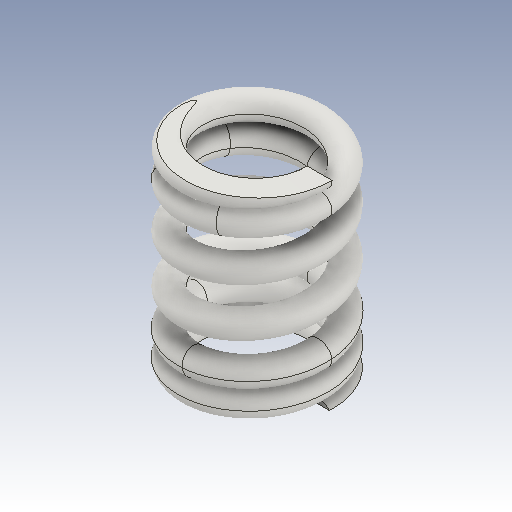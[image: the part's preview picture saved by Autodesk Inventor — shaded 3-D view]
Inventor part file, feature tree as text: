
AUTODESK INVENTOR PART (.ipt)
format: ipt  version: 2023.3 (Build 273359000, 359)  size: 781,824 bytes
history: native  units: mm
features: other x65, extrude x8, plane x5, helix x3, sketch x3, sweep x2
ambient origin geometry x8: Origin, YZ Plane, XZ Plane, XY Plane, X Axis, Y Axis, Z Axis, Center Point
bodies: Solid1 (feature_tree)
feature tree (86):
  other  "Hauptschraubenpfad(Rechts)"
  other  "Profilarbeitsebene(Rechts)"
  plane  "Arbeitsebene(Rechts) starten"
  plane  "Arbeitsebene(Rechts) beenden"
  other  "Schnittarbeitsebene(Rechts) beenden"
  other  "Schnittarbeitsebene(Rechts) starten"
  other  "Schnittarbeitsebene mit flachen Enden 1(Rechts)"
  other  "Schnittarbeitsebene mit flachen Enden 2(Rechts)"
  sweep  "Main Coil Feature(R)"
  other  "Übergangsschraube 1(Rechts) starten"
  helix  "Coil  Start Transition 2(R)"  [1 undecoded]
  helix  "Coil  Start Transition 3(R)"  [1 undecoded]
  helix  "Coil  Start Transition 4(R)"  [1 undecoded]
  other  "Endenschraube(Rechts) starten"
  extrude  "Schnittelement(Rechts) starten"  Depth=10.0mm
  other  "Übergangsschraube 1(Rechts) beenden"
  other  "Übergangsschraube 2(Rechts) beenden"
  other  "Übergangsschraube 3(Rechts) beenden"
  other  "Übergangsschraube 4(Rechts) beenden"
  other  "Spirale(Rechts) beenden"
  extrude  "Schnittelement(Rechts) beenden"  Depth=10.0mm
  extrude  "Schnittelement mit flachen Enden 1(Rechts)"  Depth=10.0mm
  extrude  "Plain Ends Cut  2(R)"  Depth=10.0mm TaperAngle=0.0deg
  other  "Hauptschraubenpfad(Links)"
  other  "Profilarbeitsebene(Links)"
  plane  "Arbeitsebene(Links) starten"
  plane  "Arbeitsebene(Links) beenden"
  other  "Schnittarbeitsebene(Links) beenden"
  other  "Schnittarbeitsebene(Links) starten"
  other  "Schnittarbeitsebene mit flachen Enden 1(Links)"
  other  "Schnittarbeitsebene mit flachen Enden 2(Links)"
  sweep  "Main Coil Feature(L)"
  other  "Übergangsschraube 1(Links) starten"
  other  "Übergangsschraube 2(Links) starten"
  other  "Übergangsschraube 3(Links) starten"
  other  "Übergangsschraube 4(Links) starten"
  other  "Endenschraube(Links) starten"
  extrude  "Schnittelement(Links) starten"  Depth=10.0mm TaperAngle=0.0deg
  other  "Übergangsschraube 1(Links) beenden"
  other  "Übergangsschraube 2(Links) beenden"
  other  "Übergangsschraube 3(Links) beenden"
  other  "Übergangsschraube 4(Links) beenden"
  other  "Spirale(Links) beenden"
  extrude  "Schnittelement(Links) beenden"  Depth=10.0mm
  extrude  "Cut Plain Ends Cut 1(L)"  TaperAngle=0.0deg  [1 undecoded]
  extrude  "Cut Plain Ends Cut 2(L)"  TaperAngle=0.0deg  [1 undecoded]
  other  "iMate-basierte Arbeitsebene"
  other  "Vorschau Mittelpunkt"
  other  "Vorschau X-Achse"
  other  "Pfadprofilskizze(Rechts)"
  other  "Srf1"
  other  "Spiralenprofilskizze(Rechts)"
  other  "Übergangsschraubenskizze 1(Rechts) starten"
  sketch  "Sketch  Start Transition 2(R)"  dims[d0=0.125mm d2=0.967126mm d3=10.0mm d4=17.5mm]
  sketch  "Sketch  Start Transition 3(R)"  dims[d5=0.0mm d6=90.0deg d7=90.0deg d8=0.0mm d9=0.0mm d12=1.006393mm d13=-1.301131mm d14=0.5mm]
  sketch  "Sketch  Start Transition 4(R)"  dims[d15=0.0mm d16=0.850345mm d17=10.0mm d18=2.5mm d19=0.0mm d20=90.0deg d21=90.0deg d22=0.0mm d23=0.0mm d24=0.733563mm d25=10.0mm d26=2.5mm d27=0.0mm d28=90.0deg d29=90.0deg d30=0.0mm d31=0.0mm d32=0.616782mm d33=10.0mm d34=2.5mm d35=0.0mm d36=90.0deg d37=90.0deg d38=0.0mm d39=0.0mm d40=0.5mm d41=10.0mm d42=2.5mm d43=0.0mm d44=90.0deg d45=90.0deg d46=0.0mm d47=0.0mm d48=0.850345mm d49=10.0mm d50=1.875mm d51=0.0mm d52=90.0deg d53=90.0deg d54=0.0mm d55=0.0mm d56=0.733563mm d57=10.0mm d58=1.875mm d59=0.0mm d60=90.0deg d61=90.0deg d62=0.0mm d63=0.0mm d64=0.616782mm d65=10.0mm d66=1.875mm d67=0.0mm d68=90.0deg d69=90.0deg d70=0.0mm d71=0.0mm d72=0.5mm d73=10.0mm d74=1.875mm d75=0.0mm d76=90.0deg d77=90.0deg d78=0.0mm d79=0.0mm d81=10.0mm d82=15.0mm d83=0.0mm d84=90.0deg d85=90.0deg d86=0.0mm d87=0.0mm d88=0.503777mm d89=10.0mm d90=10.0mm d91=0.0mm d92=90.0deg d93=90.0deg d94=0.0mm d95=0.0mm d96=3.0mm d97=0.503777mm d98=0.0mm d99=3.0mm d100=0.503777mm d101=0.0mm d102=0.0mm d103=0.0mm d104=0.0mm d105=0.0mm d106=0.0mm d108=0.0mm d112=0.0mm d113=0.0mm d114=0.0mm d121=0.129706mm d131=0.0mm d132=0.0mm d133=0.0mm d134=0.0mm d135=0.125mm d137=0.967126mm d138=10.0mm d139=17.5mm d140=0.0mm d141=90.0deg d142=90.0deg d143=0.0mm d144=0.0mm d145=1.006393mm d146=-1.301131mm d147=0.129706mm d148=0.003762mm d149=0.5mm d150=0.0mm d151=0.0mm d152=0.850345mm d153=10.0mm d154=2.5mm d155=0.0mm d156=90.0deg d157=90.0deg d158=0.0mm d159=0.0mm d160=0.733563mm d161=10.0mm d162=2.5mm d163=0.0mm d164=90.0deg d165=90.0deg d166=0.0mm d167=0.0mm d168=0.616782mm d169=10.0mm d170=2.5mm d171=0.0mm d172=90.0deg d173=90.0deg d174=0.0mm d175=0.0mm d176=0.5mm d177=10.0mm d178=2.5mm d179=0.0mm d180=90.0deg d181=90.0deg d182=0.0mm d183=0.0mm d184=10.0mm d185=10.0mm d186=10.0mm d187=10.0mm d188=0.503777mm d189=10.0mm d190=15.0mm d191=0.0mm d192=90.0deg d193=90.0deg d194=0.0mm d195=0.0mm d196=10.0mm d197=3.0mm d198=0.503777mm d199=0.0mm d200=10.0mm d201=0.850345mm d202=10.0mm d203=1.875mm d204=0.0mm d205=90.0deg d206=90.0deg d207=0.0mm d208=0.0mm d209=10.0mm d210=0.733563mm d211=10.0mm d212=1.875mm d213=0.0mm d214=90.0deg d215=90.0deg d216=0.0mm d217=0.0mm d218=0.616782mm d219=10.0mm d220=1.875mm d221=0.0mm d222=90.0deg d223=90.0deg d224=0.0mm d225=0.0mm d226=0.5mm d227=10.0mm d228=1.875mm d229=0.0mm d230=90.0deg d231=90.0deg d232=0.0mm d233=0.0mm d234=10.0mm d235=10.0mm d236=10.0mm d237=0.503777mm d238=10.0mm d239=10.0mm d240=0.0mm d241=90.0deg d242=90.0deg d243=0.0mm d244=0.0mm d245=3.0mm d246=0.503777mm d247=0.0mm d248=10.0mm d249=10.0mm d254=3.0mm d255=10.0mm d256=0.0mm d257=20.0mm d258=-0.003762mm d259=3.0mm d260=10.0mm d261=0.0mm d262=10.0mm d263=3.0mm d264=10.0mm d265=0.0mm d266=10.0mm d267=0.0mm d270=-1.238631mm d271=0.0mm d272=3.0mm d273=10.0mm d274=0.0mm d275=20.0mm d276=-157.079633mm d277=2.5mm d278=2.5mm d279=0.0mm d280=0.0mm]
  other  "Übergangsschraubenskizze 1(Rechts) beenden"
  other  "Übergangsschraubenskizze 2(Rechts) beenden"
  other  "Übergangsschraubenskizze 3(Rechts) beenden"
  other  "Übergangsschraubenskizze 4(Rechts) beenden"
  other  "Endenskizze(Rechts) starten"
  other  "Spiralenskizze(Rechts) beenden"
  other  "Schnittskizze(Rechts) beenden"
  other  "Schnittskizze (Rechts) starten"
  other  "Pfadprofilskizze(Links)"
  other  "Srf2"
  other  "Spiralenprofilskizze(Links)"
  other  "Übergangsschraubenskizze 1(Links) starten"
  other  "Übergangsschraubenskizze 2(Links) starten"
  other  "Übergangsschraubenskizze 3(Links) starten"
  other  "Übergangsschraubenskizze 4(Links) starten"
  other  "Endenskizze(Links) starten"
  other  "Schnittskizze(Links) starten"
  other  "Übergangsschraubenskizze 1(Links) beenden"
  other  "Übergangsschraubenskizze 2(Links) beenden"
  other  "Übergangsschraubenskizze 3(Links) beenden"
  other  "Übergangsschraubenskizze 4(Links) beenden"
  other  "Spiralenskizze(Links) beenden"
  other  "Schnittskizze(Links) beenden"
  other  "Schnittskizze mit flachen Enden 2(Links)"
  other  "Schnittskizze mit flachen Enden 2(Rechts)"
  other  "Schnittskizze mit flachen Enden 1(Rechts)"
  other  "Schnittskizze mit flachen Enden 1(Links)"
  plane  "Arbeitsebene - Schnitt starten"
  other  "Basiskurve(Rechts)"
  other  "Basiskurve(Links)"
note: 5 required parameter values undecoded (feature->parameter linkage not recoverable at this tier; creation-order binding heuristic only, values carry confidence <= 0.55)
